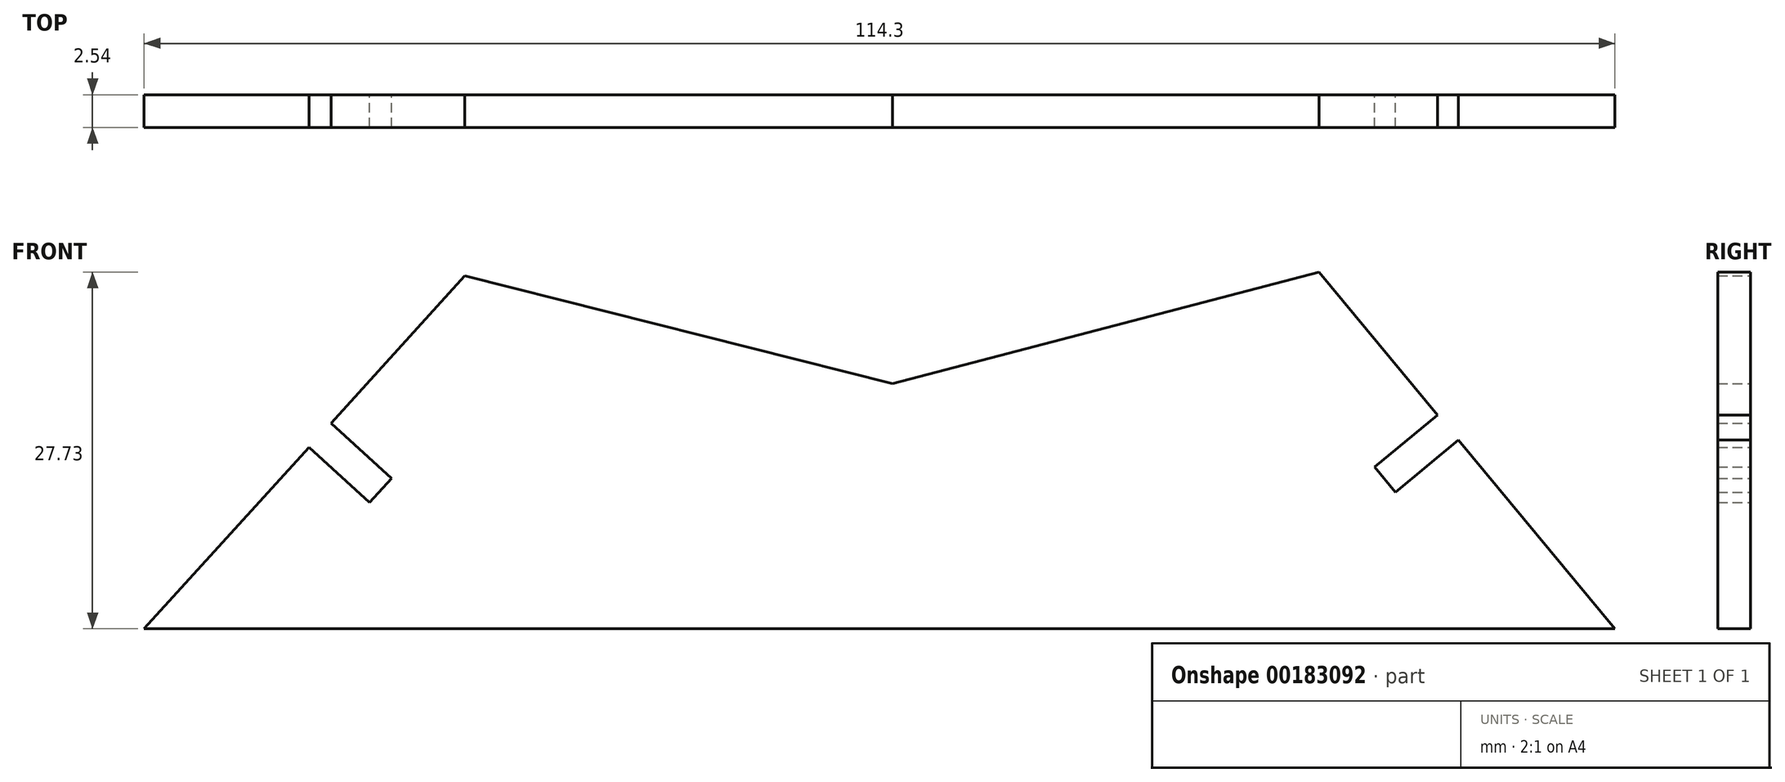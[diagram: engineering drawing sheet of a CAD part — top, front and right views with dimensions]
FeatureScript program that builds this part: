
annotation { "Feature Type Name" : "Feature", "Feature Type Description" : "" }
export const myFeature = defineFeature(function(context is Context, id is Id, definition is map)
    precondition{}
    {
        {
            var Q0;
            Q0=qCreatedBy(makeId("Front.planeOp"),FACE);
            var sketch = newSketch(context, id + "F0", { "sketchPlane" : qUnion([Q0])});
            skLineSegment(sketch, "E0", {"start": v(0, 0) * mm, "end": v(33.16, 8.68) * mm});
            skLineSegment(sketch, "E1", {"start": v(33.16, 8.68) * mm, "end": v(42.36, -2.43) * mm});
            skLineSegment(sketch, "E2", {"start": v(56.14, -19.05) * mm, "end": v(-58.16, -19.05) * mm});
            skLineSegment(sketch, "E3", {"start": v(-58.16, -19.05) * mm, "end": v(-45.35, -4.95) * mm});
            skLineSegment(sketch, "E4", {"start": v(-33.24, 8.38) * mm, "end": v(0, 0) * mm});
            skLineSegment(sketch, "E5", {"start": v(-45.35, -4.95) * mm, "end": v(-40.65, -9.22) * mm});
            skLineSegment(sketch, "E6", {"start": v(-40.65, -9.22) * mm, "end": v(-38.94, -7.34) * mm});
            skLineSegment(sketch, "E7", {"start": v(-38.94, -7.34) * mm, "end": v(-43.64, -3.07) * mm});
            skLineSegment(sketch, "E8", {"start": v(42.36, -2.43) * mm, "end": v(37.47, -6.48) * mm});
            skLineSegment(sketch, "E9", {"start": v(37.47, -6.48) * mm, "end": v(39.1, -8.43) * mm});
            skLineSegment(sketch, "E10", {"start": v(39.1, -8.43) * mm, "end": v(43.98, -4.38) * mm});
            skLineSegment(sketch, "E11.trimOffspring", {"start": v(-43.64, -3.07) * mm, "end": v(-33.24, 8.38) * mm});
            skLineSegment(sketch, "E12.trimOffspring", {"start": v(43.98, -4.38) * mm, "end": v(56.14, -19.05) * mm});
            skSolve(sketch);
        }
        {
            var Q0;
            Q0=qSketchRegion(id+"F0",true);
            extrude(context, id + "F1", {"entities" : qUnion([Q0]), "depth" : 2.54 * mm});
        }
    });
